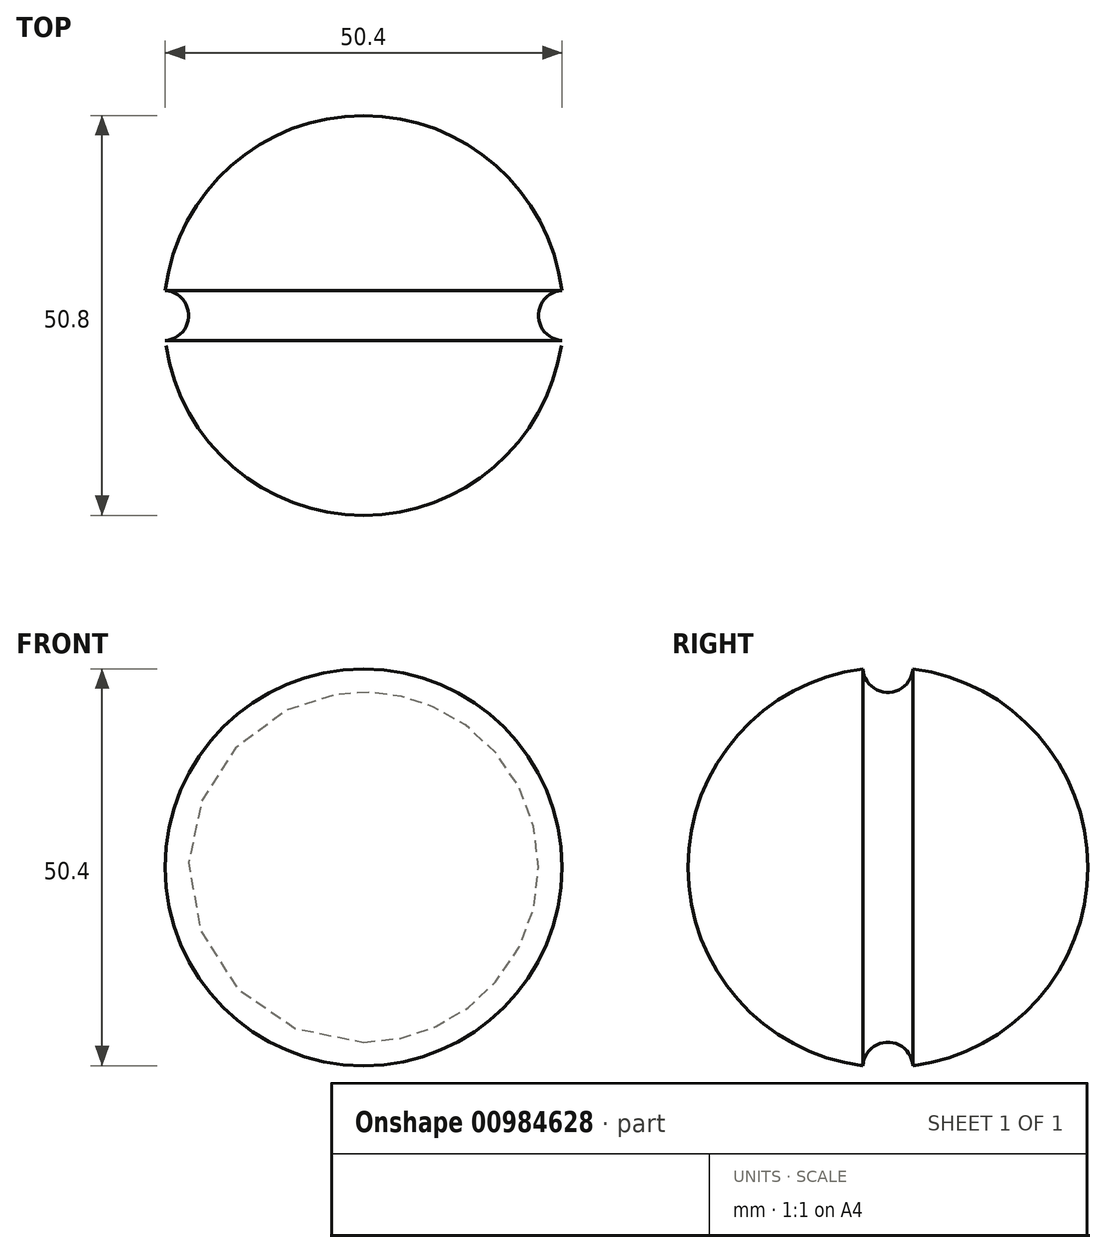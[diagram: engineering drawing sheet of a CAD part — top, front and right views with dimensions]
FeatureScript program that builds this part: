
annotation { "Feature Type Name" : "Feature", "Feature Type Description" : "" }
export const myFeature = defineFeature(function(context is Context, id is Id, definition is map)
    precondition{}
    {
        {
            var Q0;
            Q0=qCreatedBy(makeId("Top.planeOp"),FACE);
            var sketch = newSketch(context, id + "F0", { "sketchPlane" : qUnion([Q0])});
            skArc(sketch, "E0", {"start": v(25.4, 0) * mm, "mid": v(0, 25.4) * mm, "end": v(-25.4, 0) * mm});
            skLineSegment(sketch, "E1", {"start": v(-25.4, 0) * mm, "end": v(0, 0) * mm});
            skLineSegment(sketch, "E2", {"start": v(25.4, 0) * mm, "end": v(0, 0) * mm});
            skLineSegment(sketch, "E3", {"start": v(0, 0) * mm, "end": v(0, 0) * mm});
            skArc(sketch, "E4", {"start": v(17.4, 0) * mm, "mid": v(-1.07, 19.89) * mm, "end": v(-19.54, 0) * mm});
            skSolve(sketch);
        }
        {
            var Q0;
            Q0 = qSketchRegion(id + "F0", true);
            var Q1;
            Q1=sQuery(id+"F0.wireOp",EDGE,"E1");
            revolve(context, id + "F1", {"surfaceOperationType" : NewSurfaceOperationType.NEW, "entities" : qUnion([Q0]), "axis" : qUnion([Q1]), "revolveType" : RevolveType.FULL});
        }
        {
            var Q0;
            Q0=qCreatedBy(makeId("Front.planeOp"),FACE);
            var sketch = newSketch(context, id + "F2", { "sketchPlane" : qUnion([Q0])});
            skArc(sketch, "E5", {"start": v(25.4, 0) * mm, "mid": v(0, 25.4) * mm, "end": v(-25.4, 0) * mm});
            skArc(sketch, "E6", {"start": v(-25.4, 0) * mm, "mid": v(0, -25.4) * mm, "end": v(25.4, 0) * mm});
            skSolve(sketch);
        }
        {
            var Q0;
            Q0=qCreatedBy(makeId("Top.planeOp"),FACE);
            var sketch = newSketch(context, id + "F3", { "sketchPlane" : qUnion([Q0])});
            skCircle(sketch, "E7", {"center": v(25.4, 0) * mm, "radius": 3.18 * mm});
            skSolve(sketch);
        }
        {
            var Q0;
            Q0=makeQuery(id+"F3.imprint","IMPRINT",FACE,{"disambiguationData":[TD([[makeQuery(id+"F3.imprint","IMPRINT",EDGE,{"derivedFrom":sQuery(id+"F3.wireOp",EDGE,"E7")}),1.0]])]});
            var Q1;
            Q1 = qConstructionFilter(qBodyType(qCreatedBy(id + "F2" ,EDGE), BodyType.WIRE), ConstructionObject.NO);
            sweep(context, id + "F4", {"operationType" : NewBodyOperationType.REMOVE, "profiles" : qUnion([Q0]), "path" : qUnion([Q1])});
        }
    });
